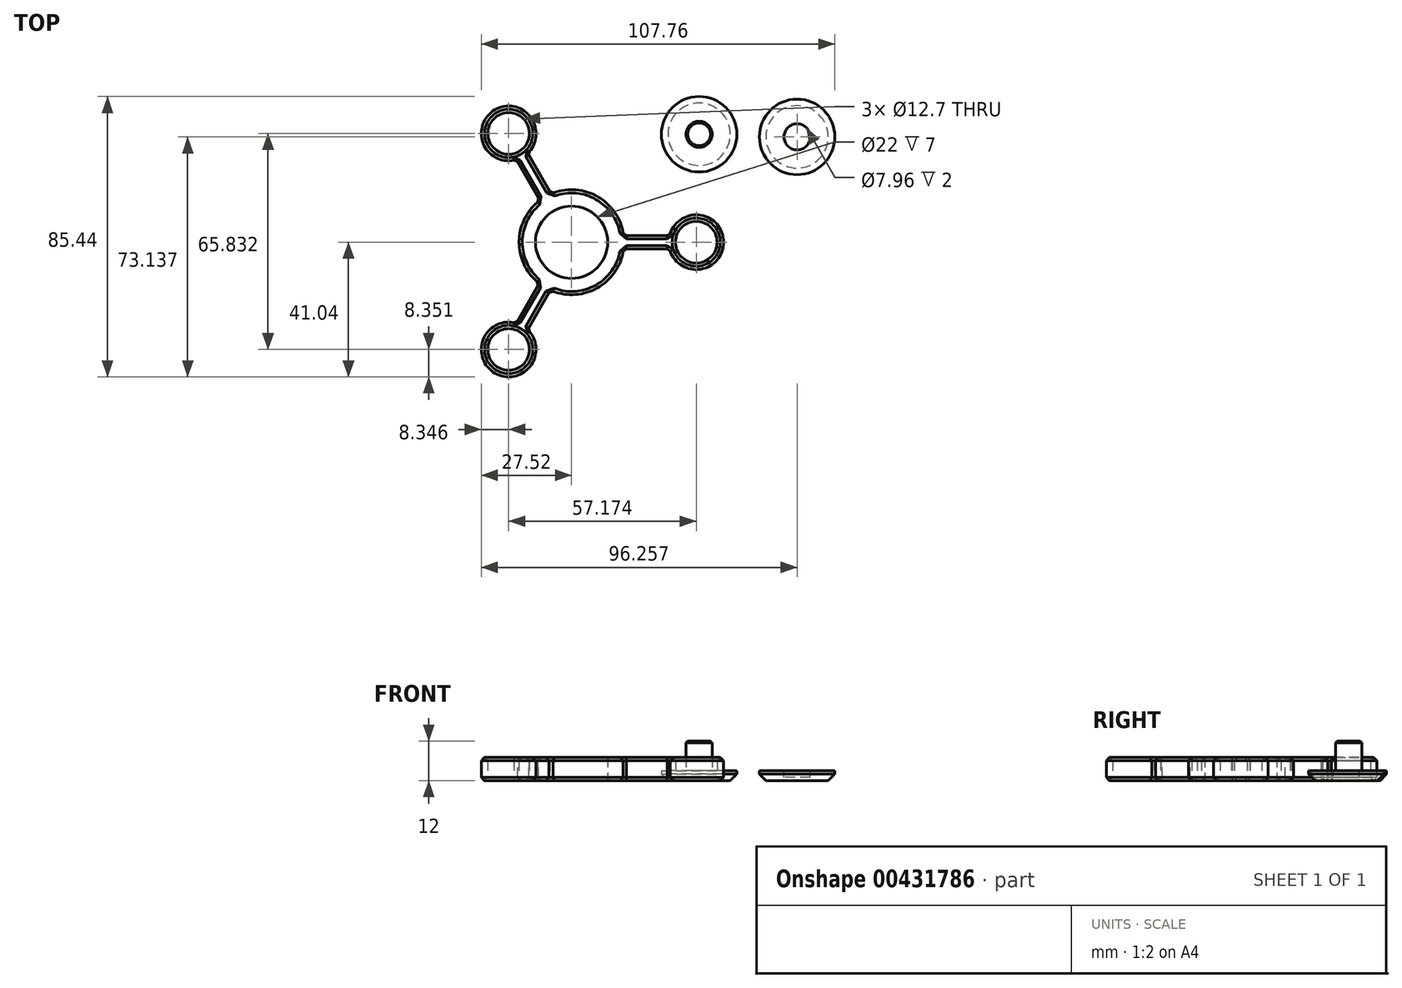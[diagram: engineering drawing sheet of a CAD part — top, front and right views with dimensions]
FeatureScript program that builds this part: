
annotation { "Feature Type Name" : "Feature", "Feature Type Description" : "" }
export const myFeature = defineFeature(function(context is Context, id is Id, definition is map)
    precondition{}
    {
        {
            var Q0;
            Q0=qCreatedBy(makeId("Top.planeOp"),FACE);
            var sketch = newSketch(context, id + "F0", { "sketchPlane" : qUnion([Q0])});
            skCircle(sketch, "E0", {"center": v(0, 0) * mm, "radius": 11 * mm});
            skCircle(sketch, "E1", {"center": v(38, 0) * mm, "radius": 6.35 * mm});
            skArc(sketch, "E2.0", {"start": v(29.9, -2) * mm, "mid": v(46.35, 0) * mm, "end": v(29.9, 2) * mm});
            skLineSegment(sketch, "E3.trimOffspring", {"start": v(15.87, 2) * mm, "end": v(29.9, 2) * mm});
            skLineSegment(sketch, "E4.trimOffspring", {"start": v(15.87, -2) * mm, "end": v(29.9, -2) * mm});
            skArc(sketch, "E5.trimOffspring", {"start": v(-15.87, -2) * mm, "mid": v(-13.92, -7.89) * mm, "end": v(-9.88, -12.59) * mm});
            skArc(sketch, "E6", {"start": v(-6.45, -14.64) * mm, "mid": v(7.89, -13.92) * mm, "end": v(15.87, -2) * mm});
            skCircle(sketch, "E7", {"center": v(-19.17, 33.14) * mm, "radius": 6.35 * mm});
            skArc(sketch, "E8.0", {"start": v(-13.39, 27.12) * mm, "mid": v(-23.35, 40.37) * mm, "end": v(-16.85, 25.12) * mm});
            skLineSegment(sketch, "E9.trimOffspring", {"start": v(-9.84, 12.98) * mm, "end": v(-16.85, 25.12) * mm});
            skCircle(sketch, "E10", {"center": v(-19.17, -32.69) * mm, "radius": 6.35 * mm});
            skArc(sketch, "E11.0", {"start": v(-16.85, -24.67) * mm, "mid": v(-23.35, -39.92) * mm, "end": v(-13.39, -26.67) * mm});
            skLineSegment(sketch, "E12.trimOffspring", {"start": v(-6.45, -14.64) * mm, "end": v(-13.39, -26.67) * mm});
            skLineSegment(sketch, "E13.trimOffspring", {"start": v(-9.88, -12.59) * mm, "end": v(-16.85, -24.67) * mm});
            skArc(sketch, "E14.trimOffspring", {"start": v(-9.7, 12.73) * mm, "mid": v(-16, 0.11) * mm, "end": v(-9.88, -12.59) * mm});
            skArc(sketch, "E15.trimOffspring", {"start": v(-6.23, 14.74) * mm, "mid": v(7.99, 13.86) * mm, "end": v(15.87, 2) * mm});
            skArc(sketch, "E16.trimOffspring", {"start": v(-9.7, 12.73) * mm, "mid": v(-13.87, 7.99) * mm, "end": v(-15.87, 2) * mm});
            skLineSegment(sketch, "E17", {"start": v(-16.85, 25.12) * mm, "end": v(-9.7, 12.73) * mm});
            skLineSegment(sketch, "E18", {"start": v(-6.23, 14.74) * mm, "end": v(-13.39, 27.12) * mm});
            skSolve(sketch);
        }
        {
            var Q0;
            Q0=makeQuery(id+"F0.imprint","IMPRINT",FACE,{"disambiguationData":[TD([[makeQuery(id+"F0.imprint","IMPRINT",EDGE,{"derivedFrom":sQuery(id+"F0.wireOp",EDGE,"E1")}),-1.0]])]});
            extrude(context, id + "F1", {"entities" : qUnion([Q0]), "depth" : 7 * mm});
        }
        {
            var Q0;
            Q0=makeQuery(id+"F1.opExtrude","CAP_EDGE",EDGE,{"disambiguationData":[OSD([sQuery(id+"F0.wireOp",EDGE,"E4.trimOffspring")])],"isStart":false});
            var Q1;
            Q1=makeQuery(id+"F1.opExtrude","CAP_EDGE",EDGE,{"disambiguationData":[OSD([sQuery(id+"F0.wireOp",EDGE,"E6")])],"isStart":false});
            var Q2;
            Q2=makeQuery(id+"F1.opExtrude","CAP_EDGE",EDGE,{"disambiguationData":[OSD([sQuery(id+"F0.wireOp",EDGE,"E12.trimOffspring")])],"isStart":false});
            var Q3;
            Q3=makeQuery(id+"F1.opExtrude","CAP_EDGE",EDGE,{"disambiguationData":[OSD([sQuery(id+"F0.wireOp",EDGE,"E13.trimOffspring")])],"isStart":false});
            var Q4;
            Q4=makeQuery(id+"F1.opExtrude","CAP_EDGE",EDGE,{"disambiguationData":[OSD([sQuery(id+"F0.wireOp",EDGE,"E11.0")])],"isStart":false});
            var Q5;
            Q5=makeQuery(id+"F1.opExtrude","CAP_EDGE",EDGE,{"disambiguationData":[OSD([sQuery(id+"F0.wireOp",EDGE,"E14.trimOffspring"),sQuery(id+"F0.wireOp",EDGE,"E16.trimOffspring")])],"isStart":false});
            var Q6;
            Q6=makeQuery(id+"F1.opExtrude","CAP_EDGE",EDGE,{"disambiguationData":[OSD([sQuery(id+"F0.wireOp",EDGE,"E15.trimOffspring")])],"isStart":false});
            var Q7;
            Q7=makeQuery(id+"F1.opExtrude","CAP_EDGE",EDGE,{"disambiguationData":[OSD([sQuery(id+"F0.wireOp",EDGE,"E3.trimOffspring")])],"isStart":false});
            var Q8;
            Q8=makeQuery(id+"F1.opExtrude","CAP_EDGE",EDGE,{"disambiguationData":[OSD([sQuery(id+"F0.wireOp",EDGE,"26c748fc-4364-43c6-b27c-564c10fa0414.trimOffspring"),sQuery(id+"F0.wireOp",EDGE,"B5oK3brW-lbyJ-Mrhh-ZTcF-0CYacTayKQtu")])],"isStart":false});
            var Q9;
            Q9=makeQuery(id+"F1.opExtrude","CAP_EDGE",EDGE,{"disambiguationData":[OSD([sQuery(id+"F0.wireOp",EDGE,"E17")])],"isStart":false});
            var Q10;
            Q10=makeQuery(id+"F1.opExtrude","CAP_EDGE",EDGE,{"disambiguationData":[OSD([sQuery(id+"F0.wireOp",EDGE,"E8.0")])],"isStart":false});
            var Q11;
            Q11=makeQuery(id+"F1.opExtrude","CAP_EDGE",EDGE,{"disambiguationData":[OSD([sQuery(id+"F0.wireOp",EDGE,"E2.0")])],"isStart":false});
            var Q12;
            Q12=makeQuery(id+"F1.opExtrude","CAP_EDGE",EDGE,{"disambiguationData":[OSD([sQuery(id+"F0.wireOp",EDGE,"E6")])],"isStart":true});
            var Q13;
            Q13=makeQuery(id+"F1.opExtrude","CAP_EDGE",EDGE,{"disambiguationData":[OSD([sQuery(id+"F0.wireOp",EDGE,"E4.trimOffspring")])],"isStart":true});
            var Q14;
            Q14=makeQuery(id+"F1.opExtrude","CAP_EDGE",EDGE,{"disambiguationData":[OSD([sQuery(id+"F0.wireOp",EDGE,"E3.trimOffspring")])],"isStart":true});
            var Q15;
            Q15=makeQuery(id+"F1.opExtrude","CAP_EDGE",EDGE,{"disambiguationData":[OSD([sQuery(id+"F0.wireOp",EDGE,"E2.0")])],"isStart":true});
            var Q16;
            Q16=makeQuery(id+"F1.opExtrude","CAP_EDGE",EDGE,{"disambiguationData":[OSD([sQuery(id+"F0.wireOp",EDGE,"E15.trimOffspring")])],"isStart":true});
            var Q17;
            Q17=makeQuery(id+"F1.opExtrude","CAP_EDGE",EDGE,{"disambiguationData":[OSD([sQuery(id+"F0.wireOp",EDGE,"26c748fc-4364-43c6-b27c-564c10fa0414.trimOffspring"),sQuery(id+"F0.wireOp",EDGE,"B5oK3brW-lbyJ-Mrhh-ZTcF-0CYacTayKQtu")])],"isStart":true});
            var Q18;
            Q18=makeQuery(id+"F1.opExtrude","CAP_EDGE",EDGE,{"disambiguationData":[OSD([sQuery(id+"F0.wireOp",EDGE,"E17")])],"isStart":true});
            var Q19;
            Q19=makeQuery(id+"F1.opExtrude","CAP_EDGE",EDGE,{"disambiguationData":[OSD([sQuery(id+"F0.wireOp",EDGE,"E8.0")])],"isStart":true});
            var Q20;
            Q20=makeQuery(id+"F1.opExtrude","CAP_EDGE",EDGE,{"disambiguationData":[OSD([sQuery(id+"F0.wireOp",EDGE,"E13.trimOffspring")])],"isStart":true});
            var Q21;
            Q21=makeQuery(id+"F1.opExtrude","CAP_EDGE",EDGE,{"disambiguationData":[OSD([sQuery(id+"F0.wireOp",EDGE,"E11.0")])],"isStart":true});
            var Q22;
            Q22=makeQuery(id+"F1.opExtrude","CAP_EDGE",EDGE,{"disambiguationData":[OSD([sQuery(id+"F0.wireOp",EDGE,"E12.trimOffspring")])],"isStart":true});
            var Q23;
            Q23=makeQuery(id+"F1.opExtrude","CAP_EDGE",EDGE,{"disambiguationData":[OSD([sQuery(id+"F0.wireOp",EDGE,"E14.trimOffspring"),sQuery(id+"F0.wireOp",EDGE,"E16.trimOffspring")])],"isStart":true});
            var Q24;
            Q24=makeQuery(id+"F1.opExtrude","SWEPT_EDGE",EDGE,{"disambiguationData":[OSD([sQuery(id+"F0.wireOp",EDGE,"E12.trimOffspring"),sQuery(id+"F0.wireOp",EDGE,"E6")])]});
            var Q25;
            Q25=makeQuery(id+"F1.opExtrude","SWEPT_EDGE",EDGE,{"disambiguationData":[OSD([sQuery(id+"F0.wireOp",EDGE,"E4.trimOffspring"),sQuery(id+"F0.wireOp",EDGE,"E6")])]});
            var Q26;
            Q26=makeQuery(id+"F1.opExtrude","SWEPT_EDGE",EDGE,{"disambiguationData":[OSD([sQuery(id+"F0.wireOp",EDGE,"E11.0"),sQuery(id+"F0.wireOp",EDGE,"E12.trimOffspring")])]});
            var Q27;
            Q27=makeQuery(id+"F1.opExtrude","SWEPT_FACE",FACE,{"disambiguationData":[OSD([sQuery(id+"F0.wireOp",EDGE,"E4.trimOffspring")])]});
            var Q28;
            Q28=makeQuery(id+"F1.opExtrude","SWEPT_EDGE",EDGE,{"disambiguationData":[OSD([sQuery(id+"F0.wireOp",EDGE,"E11.0"),sQuery(id+"F0.wireOp",EDGE,"E13.trimOffspring")])]});
            var Q29;
            Q29=makeQuery(id+"F1.opExtrude","SWEPT_EDGE",EDGE,{"disambiguationData":[OSD([sQuery(id+"F0.wireOp",EDGE,"E13.trimOffspring"),sQuery(id+"F0.wireOp",EDGE,"E14.trimOffspring")])]});
            var Q30;
            Q30=makeQuery(id+"F1.opExtrude","SWEPT_EDGE",EDGE,{"disambiguationData":[OSD([sQuery(id+"F0.wireOp",EDGE,"E16.trimOffspring"),sQuery(id+"F0.wireOp",EDGE,"E17")])]});
            var Q31;
            Q31=makeQuery(id+"F1.opExtrude","SWEPT_EDGE",EDGE,{"disambiguationData":[OSD([sQuery(id+"F0.wireOp",EDGE,"GuP0xdWu-ipNW-Yx1U-0fVq-GBnKM3Klz6Yp"),sQuery(id+"F0.wireOp",EDGE,"B5oK3brW-lbyJ-Mrhh-ZTcF-0CYacTayKQtu")])]});
            var Q32;
            Q32=makeQuery(id+"F1.opExtrude","SWEPT_EDGE",EDGE,{"disambiguationData":[OSD([sQuery(id+"F0.wireOp",EDGE,"E3.trimOffspring"),sQuery(id+"F0.wireOp",EDGE,"E15.trimOffspring")])]});
            var Q33;
            Q33=makeQuery(id+"F1.opExtrude","SWEPT_EDGE",EDGE,{"disambiguationData":[OSD([sQuery(id+"F0.wireOp",EDGE,"E8.0"),sQuery(id+"F0.wireOp",EDGE,"26c748fc-4364-43c6-b27c-564c10fa0414.trimOffspring")])]});
            var Q34;
            Q34=makeQuery(id+"F1.opExtrude","SWEPT_EDGE",EDGE,{"disambiguationData":[OSD([sQuery(id+"F0.wireOp",EDGE,"E2.0"),sQuery(id+"F0.wireOp",EDGE,"E3.trimOffspring")])]});
            var Q35;
            Q35=makeQuery(id+"F1.opExtrude","SWEPT_FACE",FACE,{"disambiguationData":[OSD([sQuery(id+"F0.wireOp",EDGE,"E17")])]});
            var Q36;
            Q36=makeQuery(id+"F1.opExtrude","SWEPT_EDGE",EDGE,{"disambiguationData":[OSD([sQuery(id+"F0.wireOp",EDGE,"GuP0xdWu-ipNW-Yx1U-0fVq-GBnKM3Klz6Yp"),sQuery(id+"F0.wireOp",EDGE,"E15.trimOffspring")])]});
            var Q37;
            Q37=makeQuery(id+"F1.opExtrude","SWEPT_FACE",FACE,{"disambiguationData":[OSD([sQuery(id+"F0.wireOp",EDGE,"E7")])]});
            var Q38;
            Q38=makeQuery(id+"F1.opExtrude","SWEPT_FACE",FACE,{"disambiguationData":[OSD([sQuery(id+"F0.wireOp",EDGE,"E10")])]});
            var Q39;
            Q39=makeQuery(id+"F1.opExtrude","CAP_EDGE",EDGE,{"disambiguationData":[OSD([sQuery(id+"F0.wireOp",EDGE,"E1")])],"isStart":false});
            var Q40;
            Q40=makeQuery(id+"F1.opExtrude","CAP_EDGE",EDGE,{"disambiguationData":[OSD([sQuery(id+"F0.wireOp",EDGE,"E1")])],"isStart":true});
            chamfer(context, id + "F2", {"entities" : qUnion([Q0, Q1, Q2, Q3, Q4, Q5, Q6, Q7, Q8, Q9, Q10, Q11, Q12, Q13, Q14, Q15, Q16, Q17, Q18, Q19, Q20, Q21, Q22, Q23, Q24, Q25, Q26, Q27, Q28, Q29, Q30, Q31, Q32, Q33, Q34, Q35, Q36, Q37, Q38, Q39, Q40]), "width" : 1 * mm, "tangentPropagation" : true});
        }
        {
            var Q0;
            Q0=qCreatedBy(makeId("Top.planeOp"),FACE);
            var sketch = newSketch(context, id + "F3", { "sketchPlane" : qUnion([Q0])});
            skCircle(sketch, "E19", {"center": v(38.88, 32.9) * mm, "radius": 11.5 * mm});
            skCircle(sketch, "E20", {"center": v(68.74, 32.1) * mm, "radius": 11.5 * mm});
            skSolve(sketch);
        }
        {
            var Q0;
            Q0=makeQuery(id+"F3.imprint","IMPRINT",FACE,{"disambiguationData":[TD([[makeQuery(id+"F3.imprint","IMPRINT",EDGE,{"derivedFrom":sQuery(id+"F3.wireOp",EDGE,"E19")}),1.0]])]});
            var Q1;
            Q1=makeQuery(id+"F3.imprint","IMPRINT",FACE,{"disambiguationData":[TD([[makeQuery(id+"F3.imprint","IMPRINT",EDGE,{"derivedFrom":sQuery(id+"F3.wireOp",EDGE,"E20")}),1.0]])]});
            extrude(context, id + "F4", {"entities" : qUnion([Q0, Q1]), "depth" : 3 * mm});
        }
        {
            var Q0;
            Q0=makeQuery(id+"F4.opExtrude","CAP_FACE",FACE,{"disambiguationData":[OSD([sQuery(id+"F3.wireOp",EDGE,"E19")])],"isStart":false});
            var sketch = newSketch(context, id + "F5", { "sketchPlane" : qUnion([Q0])});
            skCircle(sketch, "E21", {"center": v(38.88, 32.9) * mm, "radius": 3.98 * mm});
            skSolve(sketch);
        }
        {
            var Q0;
            Q0=makeQuery(id+"F5.imprint","IMPRINT",FACE,{"disambiguationData":[TD([[makeQuery(id+"F5.imprint","IMPRINT",EDGE,{"derivedFrom":sQuery(id+"F5.wireOp",EDGE,"E21")}),1.0]])]});
            extrude(context, id + "F6", {"entities" : qUnion([Q0]), "operationType" : NewBodyOperationType.ADD, "depth" : 9 * mm});
        }
        {
            var Q0;
            Q0=makeQuery(id+"F4.opExtrude","CAP_FACE",FACE,{"disambiguationData":[OSD([sQuery(id+"F3.wireOp",EDGE,"E20")])],"isStart":false});
            var sketch = newSketch(context, id + "F7", { "sketchPlane" : qUnion([Q0])});
            skCircle(sketch, "E22", {"center": v(68.74, 32.1) * mm, "radius": 3.98 * mm});
            skSolve(sketch);
        }
        {
            var Q0;
            Q0=makeQuery(id+"F7.imprint","IMPRINT",FACE,{"disambiguationData":[TD([[makeQuery(id+"F7.imprint","IMPRINT",EDGE,{"derivedFrom":sQuery(id+"F7.wireOp",EDGE,"E22")}),1.0]])]});
            extrude(context, id + "F8", {"entities" : qUnion([Q0]), "operationType" : NewBodyOperationType.REMOVE, "oppositeDirection" : true, "depth" : 2 * mm});
        }
        {
            var Q0;
            Q0=makeQuery(id+"F6.opExtrude","CAP_EDGE",EDGE,{"disambiguationData":[OSD([sQuery(id+"F5.wireOp",EDGE,"E21")])],"isStart":false});
            chamfer(context, id + "F9", {"entities" : qUnion([Q0]), "width" : .5 * mm, "tangentPropagation" : true});
        }
        {
            var Q0;
            Q0=makeQuery(id+"F4.opExtrude","CAP_EDGE",EDGE,{"disambiguationData":[OSD([sQuery(id+"F3.wireOp",EDGE,"E20")])],"isStart":true});
            var Q1;
            Q1=makeQuery(id+"F4.opExtrude","CAP_EDGE",EDGE,{"disambiguationData":[OSD([sQuery(id+"F3.wireOp",EDGE,"E19")])],"isStart":true});
            chamfer(context, id + "F10", {"entities" : qUnion([Q0, Q1]), "width" : 2 * mm, "tangentPropagation" : true});
        }
    });
